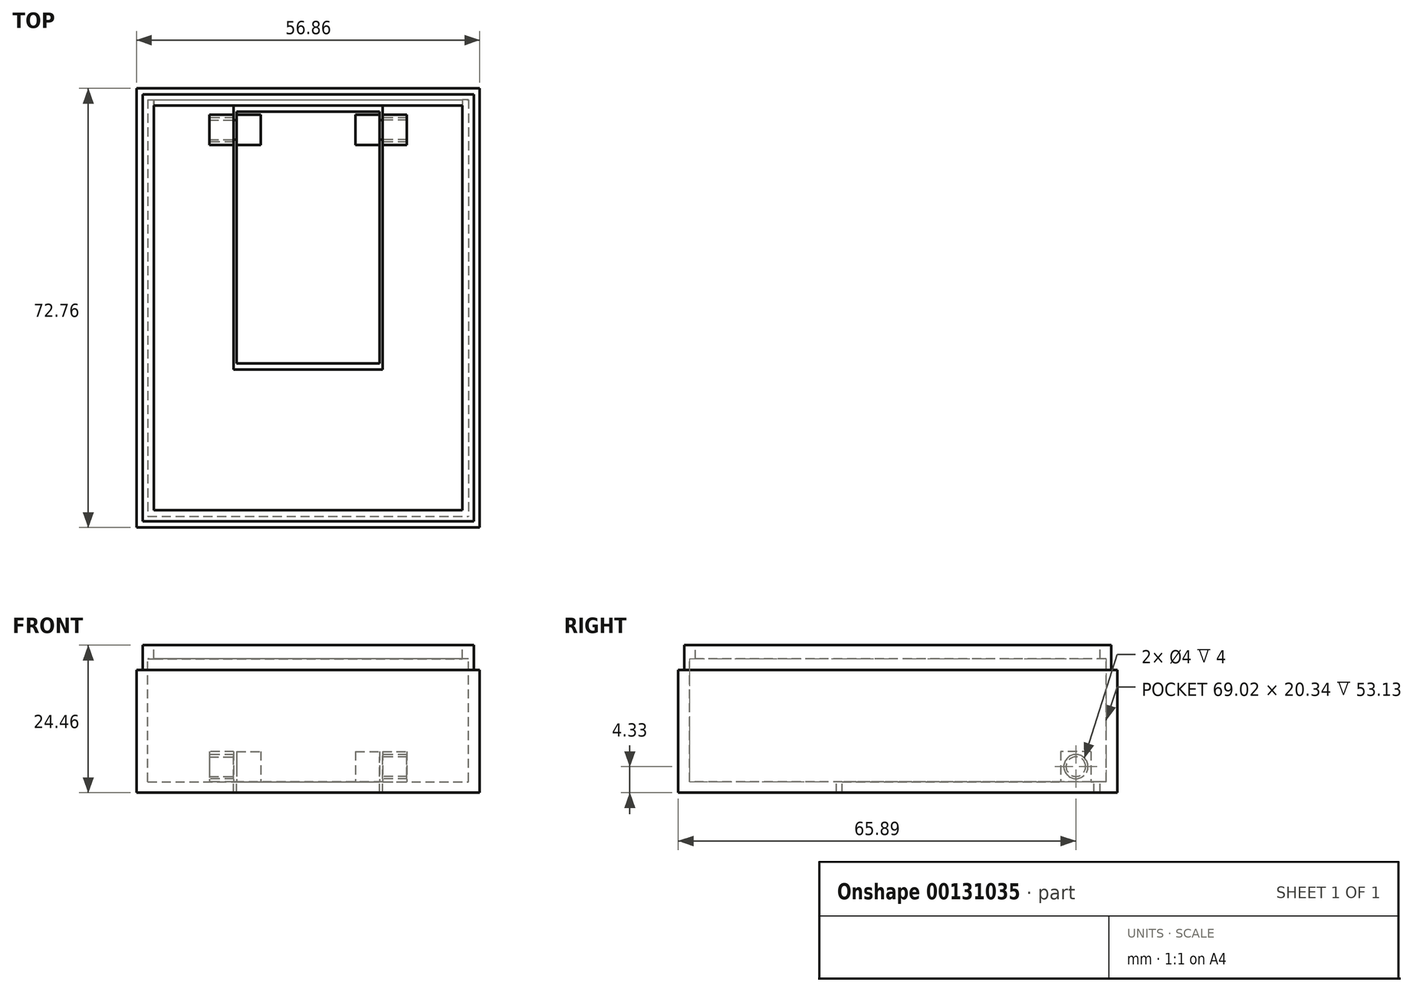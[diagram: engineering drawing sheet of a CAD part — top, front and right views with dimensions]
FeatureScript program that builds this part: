
annotation { "Feature Type Name" : "Feature", "Feature Type Description" : "" }
export const myFeature = defineFeature(function(context is Context, id is Id, definition is map)
    precondition{}
    {
        {
            var Q0;
            Q0=qCreatedBy(makeId("Front.planeOp"),FACE);
            var sketch = newSketch(context, id + "F0", { "sketchPlane" : qUnion([Q0])});
            skLineSegment(sketch, "E0.bottom", {"start": v(-28.43, 12.23) * mm, "end": v(28.44, 12.23) * mm});
            skLineSegment(sketch, "E0.top", {"start": v(-28.44, -12.23) * mm, "end": v(28.43, -12.23) * mm});
            skLineSegment(sketch, "E0.left", {"start": v(-28.43, 12.23) * mm, "end": v(-28.44, -12.23) * mm});
            skLineSegment(sketch, "E0.right", {"start": v(28.44, 12.23) * mm, "end": v(28.43, -12.23) * mm});
            skPoint(sketch, "E0.middle", {"position": v(0, 0) * mm});
            skSolve(sketch);
        }
        {
            var Q0;
            Q0 = qSketchRegion(id + "F0", true);
            extrude(context, id + "F1", {"entities" : qUnion([Q0]), "endBound" : BoundingType.SYMMETRIC, "depth" : 72.76 * mm});
        }
        {
            var Q0;
            Q0=makeQuery(id+"F1.opExtrude","SWEPT_FACE",FACE,{"disambiguationData":[OSD([sQuery(id+"F0.wireOp",EDGE,"E0.bottom")])]});
            var sketch = newSketch(context, id + "F2", { "sketchPlane" : qUnion([Q0])});
            skLineSegment(sketch, "E1.bottom", {"start": v(-25.57, 33.51) * mm, "end": v(25.57, 33.51) * mm});
            skLineSegment(sketch, "E1.top", {"start": v(-25.57, -33.51) * mm, "end": v(25.57, -33.51) * mm});
            skLineSegment(sketch, "E1.left", {"start": v(-25.57, 33.51) * mm, "end": v(-25.57, -33.51) * mm});
            skLineSegment(sketch, "E1.right", {"start": v(25.57, 33.51) * mm, "end": v(25.57, -33.51) * mm});
            skPoint(sketch, "E1.middle", {"position": v(0, 0) * mm});
            skSolve(sketch);
        }
        {
            var Q0;
            Q0 = qSketchRegion(id + "F2", true);
            extrude(context, id + "F3", {"entities" : qUnion([Q0]), "operationType" : NewBodyOperationType.REMOVE, "oppositeDirection" : true, "depth" : 22.63 * mm});
        }
        {
            var Q0;
            Q0=makeQuery(id+"F3.boolean.opBoolean","COPY",FACE,{"derivedFrom":makeQuery(id+"F3.opExtrude","SWEPT_FACE",FACE,{"disambiguationData":[OSD([sQuery(id+"F2.wireOp",EDGE,"E1.bottom")])]})});
            var sketch = newSketch(context, id + "F4", { "sketchPlane" : qUnion([Q0])});
            skLineSegment(sketch, "E2.bottom", {"start": v(-25.57, -10.4) * mm, "end": v(25.57, -10.4) * mm});
            skLineSegment(sketch, "E2.top", {"start": v(-25.57, 9.96) * mm, "end": v(25.57, 9.96) * mm});
            skLineSegment(sketch, "E2.left", {"start": v(-25.57, -10.4) * mm, "end": v(-25.57, 9.96) * mm});
            skLineSegment(sketch, "E2.right", {"start": v(25.57, -10.4) * mm, "end": v(25.57, 9.96) * mm});
            skSolve(sketch);
        }
        {
            var Q0;
            Q0 = qSketchRegion(id + "F4", true);
            extrude(context, id + "F5", {"entities" : qUnion([Q0]), "operationType" : NewBodyOperationType.REMOVE, "oppositeDirection" : true, "depth" : 1 * mm});
        }
        {
            var Q0;
            Q0=makeQuery(id+"F5.boolean.opBoolean","MERGE",FACE,{"derivedFrom":[makeQuery(id+"F3.boolean.opBoolean","COPY",FACE,{"derivedFrom":makeQuery(id+"F3.opExtrude","SWEPT_FACE",FACE,{"disambiguationData":[OSD([sQuery(id+"F2.wireOp",EDGE,"E1.left")])]})}),makeQuery(id+"F5.opExtrude","SWEPT_FACE",FACE,{"disambiguationData":[OSD([sQuery(id+"F4.wireOp",EDGE,"E2.left")])]})]});
            var sketch = newSketch(context, id + "F6", { "sketchPlane" : qUnion([Q0])});
            skLineSegment(sketch, "E3.bottom", {"start": v(-33.51, -10.4) * mm, "end": v(34.51, -10.4) * mm});
            skLineSegment(sketch, "E3.top", {"start": v(-33.51, 9.94) * mm, "end": v(34.51, 9.94) * mm});
            skLineSegment(sketch, "E3.left", {"start": v(-33.51, -10.4) * mm, "end": v(-33.51, 9.94) * mm});
            skLineSegment(sketch, "E3.right", {"start": v(34.51, -10.4) * mm, "end": v(34.51, 9.94) * mm});
            skSolve(sketch);
        }
        {
            var Q0;
            Q0 = qSketchRegion(id + "F6", true);
            extrude(context, id + "F7", {"entities" : qUnion([Q0]), "operationType" : NewBodyOperationType.REMOVE, "oppositeDirection" : true, "depth" : 1 * mm});
        }
        {
            var Q0;
            Q0=makeQuery(id+"F7.boolean.opBoolean","MERGE",FACE,{"derivedFrom":[makeQuery(id+"F3.boolean.opBoolean","COPY",FACE,{"derivedFrom":makeQuery(id+"F3.opExtrude","SWEPT_FACE",FACE,{"disambiguationData":[OSD([sQuery(id+"F2.wireOp",EDGE,"E1.top")])]})}),makeQuery(id+"F7.opExtrude","SWEPT_FACE",FACE,{"disambiguationData":[OSD([sQuery(id+"F6.wireOp",EDGE,"E3.left")])]})]});
            var sketch = newSketch(context, id + "F8", { "sketchPlane" : qUnion([Q0])});
            skLineSegment(sketch, "E4.bottom", {"start": v(-25.57, -10.4) * mm, "end": v(26.57, -10.4) * mm});
            skLineSegment(sketch, "E4.top", {"start": v(-25.57, 9.94) * mm, "end": v(26.57, 9.94) * mm});
            skLineSegment(sketch, "E4.left", {"start": v(-25.57, -10.4) * mm, "end": v(-25.57, 9.94) * mm});
            skLineSegment(sketch, "E4.right", {"start": v(26.57, -10.4) * mm, "end": v(26.57, 9.94) * mm});
            skSolve(sketch);
        }
        {
            var Q0;
            Q0 = qSketchRegion(id + "F8", true);
            extrude(context, id + "F9", {"entities" : qUnion([Q0]), "operationType" : NewBodyOperationType.REMOVE, "oppositeDirection" : true, "depth" : 1 * mm});
        }
        {
            var Q0;
            Q0=makeQuery(id+"F9.boolean.opBoolean","MERGE",FACE,{"derivedFrom":[makeQuery(id+"F5.boolean.opBoolean","MERGE",FACE,{"derivedFrom":[makeQuery(id+"F3.boolean.opBoolean","COPY",FACE,{"derivedFrom":makeQuery(id+"F3.opExtrude","SWEPT_FACE",FACE,{"disambiguationData":[OSD([sQuery(id+"F2.wireOp",EDGE,"E1.right")])]})}),makeQuery(id+"F5.opExtrude","SWEPT_FACE",FACE,{"disambiguationData":[OSD([sQuery(id+"F4.wireOp",EDGE,"E2.right")])]})]}),makeQuery(id+"F9.opExtrude","SWEPT_FACE",FACE,{"disambiguationData":[OSD([sQuery(id+"F8.wireOp",EDGE,"E4.left")])]})]});
            var sketch = newSketch(context, id + "F10", { "sketchPlane" : qUnion([Q0])});
            skLineSegment(sketch, "E5.bottom", {"start": v(-34.51, -10.4) * mm, "end": v(34.51, -10.4) * mm});
            skLineSegment(sketch, "E5.top", {"start": v(-34.51, 9.94) * mm, "end": v(34.51, 9.94) * mm});
            skLineSegment(sketch, "E5.left", {"start": v(-34.51, -10.4) * mm, "end": v(-34.51, 9.94) * mm});
            skLineSegment(sketch, "E5.right", {"start": v(34.51, -10.4) * mm, "end": v(34.51, 9.94) * mm});
            skSolve(sketch);
        }
        {
            var Q0;
            Q0 = qSketchRegion(id + "F10", true);
            extrude(context, id + "F11", {"entities" : qUnion([Q0]), "operationType" : NewBodyOperationType.REMOVE, "oppositeDirection" : true, "depth" : 1 * mm});
        }
        {
            var Q0;
            Q0=makeQuery(id+"F1.opExtrude","SWEPT_FACE",FACE,{"disambiguationData":[OSD([sQuery(id+"F0.wireOp",EDGE,"E0.bottom")])]});
            var sketch = newSketch(context, id + "F12", { "sketchPlane" : qUnion([Q0])});
            skLineSegment(sketch, "E6.bottom", {"start": v(-27.43, 35.38) * mm, "end": v(27.43, 35.38) * mm});
            skLineSegment(sketch, "E6.top", {"start": v(-27.43, -35.38) * mm, "end": v(27.44, -35.38) * mm});
            skLineSegment(sketch, "E6.left", {"start": v(-27.43, 35.38) * mm, "end": v(-27.43, -35.38) * mm});
            skLineSegment(sketch, "E6.right", {"start": v(27.43, 35.38) * mm, "end": v(27.44, -35.38) * mm});
            skLineSegment(sketch, "E7.bottom", {"start": v(-28.43, 36.38) * mm, "end": v(28.44, 36.38) * mm});
            skLineSegment(sketch, "E7.top", {"start": v(-28.43, -36.38) * mm, "end": v(28.44, -36.38) * mm});
            skLineSegment(sketch, "E7.left", {"start": v(-28.43, 36.38) * mm, "end": v(-28.43, -36.38) * mm});
            skLineSegment(sketch, "E7.right", {"start": v(28.44, 36.38) * mm, "end": v(28.44, -36.38) * mm});
            skSolve(sketch);
        }
        {
            var Q0;
            Q0 = qSketchRegion(id + "F12", true);
            extrude(context, id + "F13", {"entities" : qUnion([Q0]), "operationType" : NewBodyOperationType.REMOVE, "oppositeDirection" : true, "depth" : 4.12 * mm});
        }
        {
            var Q0;
            Q0=makeQuery(id+"F11.boolean.opBoolean","MERGE",FACE,{"derivedFrom":[makeQuery(id+"F9.boolean.opBoolean","MERGE",FACE,{"derivedFrom":[makeQuery(id+"F7.boolean.opBoolean","MERGE",FACE,{"derivedFrom":[makeQuery(id+"F5.boolean.opBoolean","MERGE",FACE,{"derivedFrom":[makeQuery(id+"F3.boolean.opBoolean","COPY",FACE,{"derivedFrom":makeQuery(id+"F3.opExtrude","CAP_FACE",FACE,{"disambiguationData":[OSD([sQuery(id+"F2.wireOp",EDGE,"E1.bottom"),sQuery(id+"F2.wireOp",EDGE,"E1.top"),sQuery(id+"F2.wireOp",EDGE,"E1.left"),sQuery(id+"F2.wireOp",EDGE,"E1.right")])],"isStart":false})}),makeQuery(id+"F5.opExtrude","SWEPT_FACE",FACE,{"disambiguationData":[OSD([sQuery(id+"F4.wireOp",EDGE,"E2.bottom")])]})]}),makeQuery(id+"F7.opExtrude","SWEPT_FACE",FACE,{"disambiguationData":[OSD([sQuery(id+"F6.wireOp",EDGE,"E3.bottom")])]})]}),makeQuery(id+"F9.opExtrude","SWEPT_FACE",FACE,{"disambiguationData":[OSD([sQuery(id+"F8.wireOp",EDGE,"E4.bottom")])]})]}),makeQuery(id+"F11.opExtrude","SWEPT_FACE",FACE,{"disambiguationData":[OSD([sQuery(id+"F10.wireOp",EDGE,"E5.bottom")])]})]});
            var sketch = newSketch(context, id + "F14", { "sketchPlane" : qUnion([Q0])});
            skLineSegment(sketch, "E8.bottom", {"start": v(12.35, 33.51) * mm, "end": v(-12.36, 33.51) * mm});
            skLineSegment(sketch, "E8.top", {"start": v(12.36, -10.2) * mm, "end": v(-12.35, -10.2) * mm});
            skLineSegment(sketch, "E8.left", {"start": v(12.35, 33.51) * mm, "end": v(12.36, -10.2) * mm});
            skLineSegment(sketch, "E8.right", {"start": v(-12.36, 33.51) * mm, "end": v(-12.35, -10.2) * mm});
            skPoint(sketch, "E8.middle", {"position": v(0, 0) * mm});
            skLineSegment(sketch, "E9.bottom", {"start": v(-11.85, -9.7) * mm, "end": v(11.86, -9.7) * mm});
            skLineSegment(sketch, "E9.top", {"start": v(-11.86, 33.01) * mm, "end": v(11.85, 33.01) * mm});
            skLineSegment(sketch, "E9.left", {"start": v(-11.85, -9.7) * mm, "end": v(-11.86, 33.01) * mm});
            skLineSegment(sketch, "E9.right", {"start": v(11.86, -9.7) * mm, "end": v(11.85, 33.01) * mm});
            skSolve(sketch);
        }
        {
            var Q0;
            Q0=makeQuery(id+"F11.boolean.opBoolean","MERGE",FACE,{"derivedFrom":[makeQuery(id+"F9.boolean.opBoolean","MERGE",FACE,{"derivedFrom":[makeQuery(id+"F7.boolean.opBoolean","MERGE",FACE,{"derivedFrom":[makeQuery(id+"F5.boolean.opBoolean","MERGE",FACE,{"derivedFrom":[makeQuery(id+"F3.boolean.opBoolean","COPY",FACE,{"derivedFrom":makeQuery(id+"F3.opExtrude","CAP_FACE",FACE,{"disambiguationData":[OSD([sQuery(id+"F2.wireOp",EDGE,"E1.bottom"),sQuery(id+"F2.wireOp",EDGE,"E1.top"),sQuery(id+"F2.wireOp",EDGE,"E1.left"),sQuery(id+"F2.wireOp",EDGE,"E1.right")])],"isStart":false})}),makeQuery(id+"F5.opExtrude","SWEPT_FACE",FACE,{"disambiguationData":[OSD([sQuery(id+"F4.wireOp",EDGE,"E2.bottom")])]})]}),makeQuery(id+"F7.opExtrude","SWEPT_FACE",FACE,{"disambiguationData":[OSD([sQuery(id+"F6.wireOp",EDGE,"E3.bottom")])]})]}),makeQuery(id+"F9.opExtrude","SWEPT_FACE",FACE,{"disambiguationData":[OSD([sQuery(id+"F8.wireOp",EDGE,"E4.bottom")])]})]}),makeQuery(id+"F11.opExtrude","SWEPT_FACE",FACE,{"disambiguationData":[OSD([sQuery(id+"F10.wireOp",EDGE,"E5.bottom")])]})]});
            var sketch = newSketch(context, id + "F15", { "sketchPlane" : qUnion([Q0])});
            skLineSegment(sketch, "E10.bottom", {"start": v(-12.36, 32.01) * mm, "end": v(-16.36, 32.01) * mm});
            skLineSegment(sketch, "E10.top", {"start": v(-12.36, 27.01) * mm, "end": v(-16.36, 27.01) * mm});
            skLineSegment(sketch, "E10.left", {"start": v(-12.36, 32.01) * mm, "end": v(-12.36, 27.01) * mm});
            skLineSegment(sketch, "E10.right", {"start": v(-16.36, 32.01) * mm, "end": v(-16.36, 27.01) * mm});
            skSolve(sketch);
        }
        {
            var Q0;
            Q0 = qSketchRegion(id + "F15", true);
            extrude(context, id + "F16", {"entities" : qUnion([Q0]), "operationType" : NewBodyOperationType.ADD, "depth" : 5 * mm});
        }
        {
            var Q0;
            Q0=makeQuery(id+"F11.boolean.opBoolean","MERGE",FACE,{"derivedFrom":[makeQuery(id+"F9.boolean.opBoolean","MERGE",FACE,{"derivedFrom":[makeQuery(id+"F7.boolean.opBoolean","MERGE",FACE,{"derivedFrom":[makeQuery(id+"F5.boolean.opBoolean","MERGE",FACE,{"derivedFrom":[makeQuery(id+"F3.boolean.opBoolean","COPY",FACE,{"derivedFrom":makeQuery(id+"F3.opExtrude","CAP_FACE",FACE,{"disambiguationData":[OSD([sQuery(id+"F2.wireOp",EDGE,"E1.bottom"),sQuery(id+"F2.wireOp",EDGE,"E1.top"),sQuery(id+"F2.wireOp",EDGE,"E1.left"),sQuery(id+"F2.wireOp",EDGE,"E1.right")])],"isStart":false})}),makeQuery(id+"F5.opExtrude","SWEPT_FACE",FACE,{"disambiguationData":[OSD([sQuery(id+"F4.wireOp",EDGE,"E2.bottom")])]})]}),makeQuery(id+"F7.opExtrude","SWEPT_FACE",FACE,{"disambiguationData":[OSD([sQuery(id+"F6.wireOp",EDGE,"E3.bottom")])]})]}),makeQuery(id+"F9.opExtrude","SWEPT_FACE",FACE,{"disambiguationData":[OSD([sQuery(id+"F8.wireOp",EDGE,"E4.bottom")])]})]}),makeQuery(id+"F11.opExtrude","SWEPT_FACE",FACE,{"disambiguationData":[OSD([sQuery(id+"F10.wireOp",EDGE,"E5.bottom")])]})]});
            var sketch = newSketch(context, id + "F17", { "sketchPlane" : qUnion([Q0])});
            skLineSegment(sketch, "E11.bottom", {"start": v(12.35, 32.01) * mm, "end": v(16.35, 32.01) * mm});
            skLineSegment(sketch, "E11.top", {"start": v(12.35, 27.01) * mm, "end": v(16.35, 27.01) * mm});
            skLineSegment(sketch, "E11.left", {"start": v(12.35, 32.01) * mm, "end": v(12.35, 27.01) * mm});
            skLineSegment(sketch, "E11.right", {"start": v(16.35, 32.01) * mm, "end": v(16.35, 27.01) * mm});
            skSolve(sketch);
        }
        {
            var Q0;
            Q0 = qSketchRegion(id + "F17", true);
            extrude(context, id + "F18", {"entities" : qUnion([Q0]), "operationType" : NewBodyOperationType.ADD, "depth" : 5 * mm});
        }
        {
            var Q0;
            Q0=makeQuery(id+"F16.opExtrude","SWEPT_FACE",FACE,{"disambiguationData":[OSD([sQuery(id+"F15.wireOp",EDGE,"E10.right")])]});
            var sketch = newSketch(context, id + "F19", { "sketchPlane" : qUnion([Q0])});
            skCircle(sketch, "E12", {"center": v(-29.51, -7.9) * mm, "radius": 2 * mm});
            skSolve(sketch);
        }
        {
            var Q0;
            Q0 = qSketchRegion(id + "F19", true);
            var Q1;
            Q1=makeQuery(id+"F18.opExtrude","SWEPT_FACE",FACE,{"disambiguationData":[OSD([sQuery(id+"F17.wireOp",EDGE,"E11.right")])]});
            extrude(context, id + "F20", {"entities" : qUnion([Q0]), "operationType" : NewBodyOperationType.REMOVE, "endBound" : BoundingType.UP_TO_SURFACE, "oppositeDirection" : true, "endBoundEntityFace" : qUnion([Q1]), "depth" : 25 * mm});
        }
        {
            var Q0;
            Q0 = qSketchRegion(id + "F14", true);
            extrude(context, id + "F21", {"entities" : qUnion([Q0]), "operationType" : NewBodyOperationType.REMOVE, "endBound" : BoundingType.THROUGH_ALL, "oppositeDirection" : true, "depth" : 25 * mm});
        }
        {
            var Q0;
            Q0=makeQuery(id+"F21.boolean.opBoolean","SPLIT",FACE,{"disambiguationData":[TD([makeQuery(id+"F21.opExtrude","SWEPT_FACE",FACE,{"disambiguationData":[OSD([sQuery(id+"F14.wireOp",EDGE,"E9.bottom")])]})])],"derivedFrom":makeQuery(id+"F11.boolean.opBoolean","MERGE",FACE,{"derivedFrom":[makeQuery(id+"F9.boolean.opBoolean","MERGE",FACE,{"derivedFrom":[makeQuery(id+"F7.boolean.opBoolean","MERGE",FACE,{"derivedFrom":[makeQuery(id+"F5.boolean.opBoolean","MERGE",FACE,{"derivedFrom":[makeQuery(id+"F3.boolean.opBoolean","COPY",FACE,{"derivedFrom":makeQuery(id+"F3.opExtrude","CAP_FACE",FACE,{"disambiguationData":[OSD([sQuery(id+"F2.wireOp",EDGE,"E1.bottom"),sQuery(id+"F2.wireOp",EDGE,"E1.top"),sQuery(id+"F2.wireOp",EDGE,"E1.left"),sQuery(id+"F2.wireOp",EDGE,"E1.right")])],"isStart":false})}),makeQuery(id+"F5.opExtrude","SWEPT_FACE",FACE,{"disambiguationData":[OSD([sQuery(id+"F4.wireOp",EDGE,"E2.bottom")])]})]}),makeQuery(id+"F7.opExtrude","SWEPT_FACE",FACE,{"disambiguationData":[OSD([sQuery(id+"F6.wireOp",EDGE,"E3.bottom")])]})]}),makeQuery(id+"F9.opExtrude","SWEPT_FACE",FACE,{"disambiguationData":[OSD([sQuery(id+"F8.wireOp",EDGE,"E4.bottom")])]})]}),makeQuery(id+"F11.opExtrude","SWEPT_FACE",FACE,{"disambiguationData":[OSD([sQuery(id+"F10.wireOp",EDGE,"E5.bottom")])]})]})});
            var sketch = newSketch(context, id + "F22", { "sketchPlane" : qUnion([Q0])});
            skLineSegment(sketch, "E13.bottom", {"start": v(-11.86, 32.01) * mm, "end": v(-7.86, 32.01) * mm});
            skLineSegment(sketch, "E13.top", {"start": v(-11.86, 27.01) * mm, "end": v(-7.86, 27.01) * mm});
            skLineSegment(sketch, "E13.left", {"start": v(-11.86, 32.01) * mm, "end": v(-11.86, 27.01) * mm});
            skLineSegment(sketch, "E13.right", {"start": v(-7.86, 32.01) * mm, "end": v(-7.86, 27.01) * mm});
            skLineSegment(sketch, "E14.bottom", {"start": v(7.85, 32.01) * mm, "end": v(11.85, 32.01) * mm});
            skLineSegment(sketch, "E14.top", {"start": v(7.85, 27.01) * mm, "end": v(11.85, 27.01) * mm});
            skLineSegment(sketch, "E14.left", {"start": v(7.85, 32.01) * mm, "end": v(7.85, 27.01) * mm});
            skLineSegment(sketch, "E14.right", {"start": v(11.85, 32.01) * mm, "end": v(11.85, 27.01) * mm});
            skSolve(sketch);
        }
        {
            var Q0;
            Q0 = qSketchRegion(id + "F22", true);
            extrude(context, id + "F23", {"entities" : qUnion([Q0]), "operationType" : NewBodyOperationType.ADD, "depth" : 5 * mm});
        }
        {
            var Q0;
            Q0=makeQuery(id+"F23.boolean.opBoolean","MERGE",FACE,{"derivedFrom":[makeQuery(id+"F21.boolean.opBoolean","COPY",FACE,{"derivedFrom":makeQuery(id+"F21.opExtrude","SWEPT_FACE",FACE,{"disambiguationData":[OSD([sQuery(id+"F14.wireOp",EDGE,"E9.left")])]})}),makeQuery(id+"F23.opExtrude","SWEPT_FACE",FACE,{"disambiguationData":[OSD([sQuery(id+"F22.wireOp",EDGE,"E13.left")])]})]});
            var sketch = newSketch(context, id + "F24", { "sketchPlane" : qUnion([Q0])});
            skCircle(sketch, "E15", {"center": v(-29.5, -7.9) * mm, "radius": 1.63 * mm});
            skSolve(sketch);
        }
        {
            var Q0;
            Q0 = qSketchRegion(id + "F24", true);
            extrude(context, id + "F25", {"entities" : qUnion([Q0]), "depth" : 4.5 * mm});
        }
        {
            var Q0;
            Q0=makeQuery(id+"F23.boolean.opBoolean","MERGE",FACE,{"derivedFrom":[makeQuery(id+"F21.boolean.opBoolean","COPY",FACE,{"derivedFrom":makeQuery(id+"F21.opExtrude","SWEPT_FACE",FACE,{"disambiguationData":[OSD([sQuery(id+"F14.wireOp",EDGE,"E9.right")])]})}),makeQuery(id+"F23.opExtrude","SWEPT_FACE",FACE,{"disambiguationData":[OSD([sQuery(id+"F22.wireOp",EDGE,"E14.right")])]})]});
            var sketch = newSketch(context, id + "F26", { "sketchPlane" : qUnion([Q0])});
            skCircle(sketch, "E16", {"center": v(29.5, -7.9) * mm, "radius": 1.63 * mm});
            skSolve(sketch);
        }
        {
            var Q0;
            Q0 = qSketchRegion(id + "F26", true);
            extrude(context, id + "F27", {"entities" : qUnion([Q0]), "operationType" : NewBodyOperationType.ADD, "depth" : 4.5 * mm});
        }
        {
            var Q0;
            Q0=makeQuery(id+"F21.boolean.opBoolean","SPLIT",FACE,{"disambiguationData":[TD([makeQuery(id+"F21.opExtrude","SWEPT_FACE",FACE,{"disambiguationData":[OSD([sQuery(id+"F14.wireOp",EDGE,"E9.bottom")])]})])],"derivedFrom":makeQuery(id+"F11.boolean.opBoolean","MERGE",FACE,{"derivedFrom":[makeQuery(id+"F9.boolean.opBoolean","MERGE",FACE,{"derivedFrom":[makeQuery(id+"F7.boolean.opBoolean","MERGE",FACE,{"derivedFrom":[makeQuery(id+"F5.boolean.opBoolean","MERGE",FACE,{"derivedFrom":[makeQuery(id+"F3.boolean.opBoolean","COPY",FACE,{"derivedFrom":makeQuery(id+"F3.opExtrude","CAP_FACE",FACE,{"disambiguationData":[OSD([sQuery(id+"F2.wireOp",EDGE,"E1.bottom"),sQuery(id+"F2.wireOp",EDGE,"E1.top"),sQuery(id+"F2.wireOp",EDGE,"E1.left"),sQuery(id+"F2.wireOp",EDGE,"E1.right")])],"isStart":false})}),makeQuery(id+"F5.opExtrude","SWEPT_FACE",FACE,{"disambiguationData":[OSD([sQuery(id+"F4.wireOp",EDGE,"E2.bottom")])]})]}),makeQuery(id+"F7.opExtrude","SWEPT_FACE",FACE,{"disambiguationData":[OSD([sQuery(id+"F6.wireOp",EDGE,"E3.bottom")])]})]}),makeQuery(id+"F9.opExtrude","SWEPT_FACE",FACE,{"disambiguationData":[OSD([sQuery(id+"F8.wireOp",EDGE,"E4.bottom")])]})]}),makeQuery(id+"F11.opExtrude","SWEPT_FACE",FACE,{"disambiguationData":[OSD([sQuery(id+"F10.wireOp",EDGE,"E5.bottom")])]})]})});
            var sketch = newSketch(context, id + "F28", { "sketchPlane" : qUnion([Q0])});
            skLineSegment(sketch, "E17.bottom", {"start": v(-11.86, 33.01) * mm, "end": v(11.85, 33.01) * mm});
            skLineSegment(sketch, "E17.top", {"start": v(-11.86, 32.51) * mm, "end": v(11.85, 32.51) * mm});
            skLineSegment(sketch, "E17.left", {"start": v(-11.86, 33.01) * mm, "end": v(-11.86, 32.51) * mm});
            skLineSegment(sketch, "E17.right", {"start": v(11.85, 33.01) * mm, "end": v(11.85, 32.51) * mm});
            skLineSegment(sketch, "E18.bottom", {"start": v(-11.85, -9.7) * mm, "end": v(11.86, -9.7) * mm});
            skLineSegment(sketch, "E18.top", {"start": v(-11.85, -9.2) * mm, "end": v(11.86, -9.2) * mm});
            skLineSegment(sketch, "E18.left", {"start": v(-11.85, -9.7) * mm, "end": v(-11.85, -9.2) * mm});
            skLineSegment(sketch, "E18.right", {"start": v(11.86, -9.7) * mm, "end": v(11.86, -9.2) * mm});
            skSolve(sketch);
        }
        {
            var Q0;
            Q0 = qSketchRegion(id + "F28", true);
            extrude(context, id + "F29", {"entities" : qUnion([Q0]), "operationType" : NewBodyOperationType.REMOVE, "endBound" : BoundingType.THROUGH_ALL, "oppositeDirection" : true, "depth" : 25 * mm});
        }
    });
